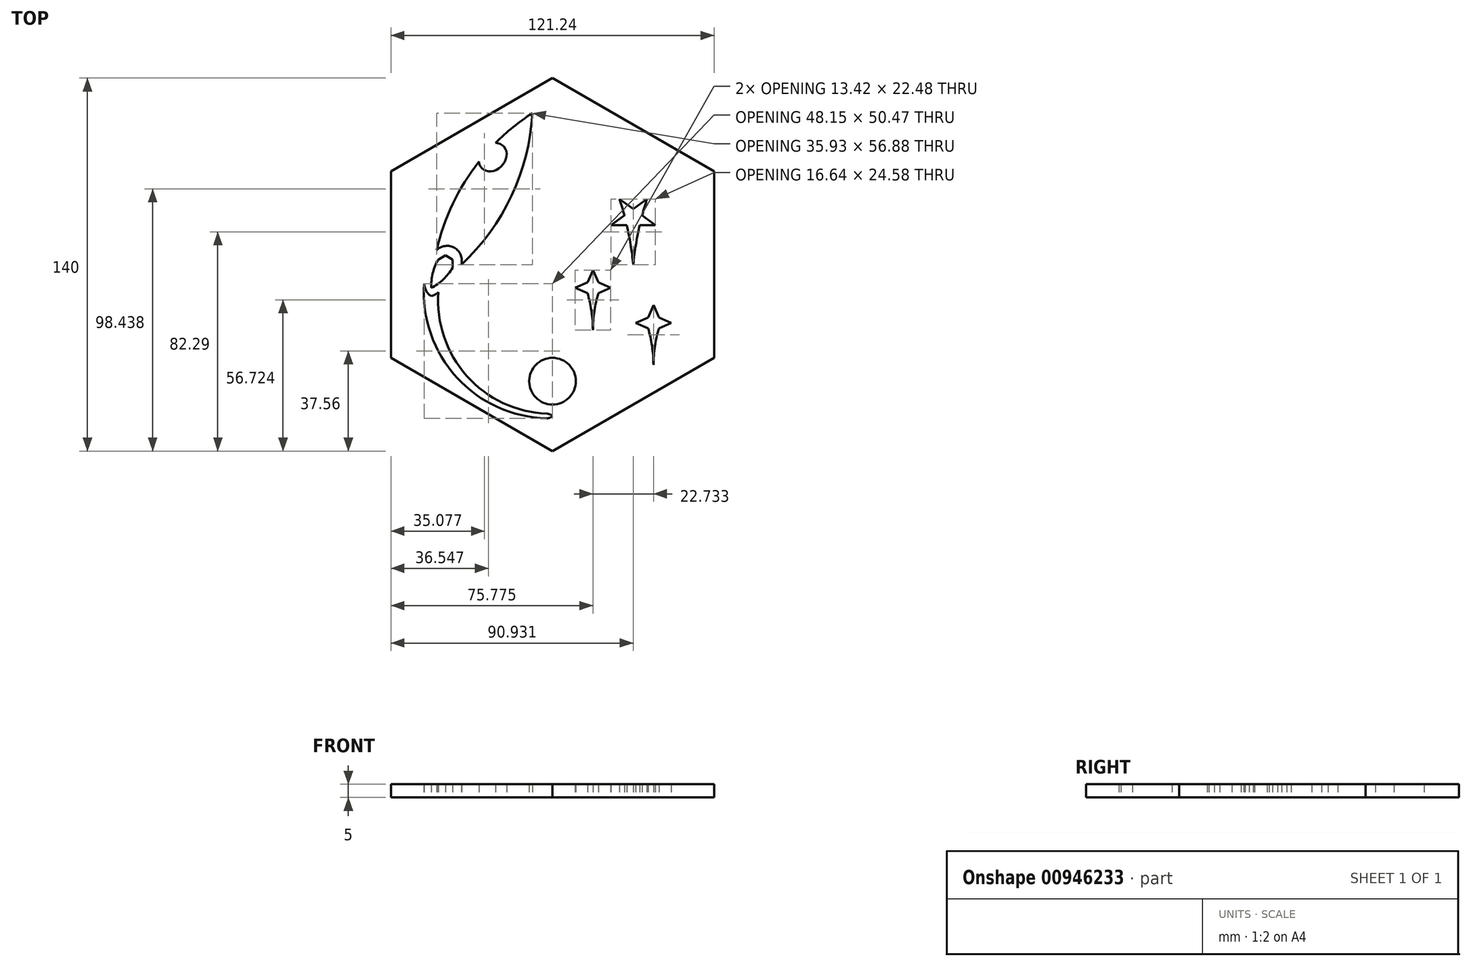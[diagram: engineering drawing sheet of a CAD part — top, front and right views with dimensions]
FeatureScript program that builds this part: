
annotation { "Feature Type Name" : "Feature", "Feature Type Description" : "" }
export const myFeature = defineFeature(function(context is Context, id is Id, definition is map)
    precondition{}
    {
        {
            var Q0;
            Q0=qCreatedBy(makeId("Top.planeOp"),FACE);
            var sketch = newSketch(context, id + "F0", { "sketchPlane" : qUnion([Q0])});
            skCircle(sketch, "E0.cCircle", {"center": v(0, 0) * mm, "radius": 60.62 * mm, "construction": true});
            skLineSegment(sketch, "E0.0", {"start": v(60.62, 35) * mm, "end": v(60.62, -35) * mm});
            skLineSegment(sketch, "E0.1", {"start": v(60.62, -35) * mm, "end": v(0, -70) * mm});
            skLineSegment(sketch, "E0.2", {"start": v(0, -70) * mm, "end": v(-60.62, -35) * mm});
            skLineSegment(sketch, "E0.3", {"start": v(-60.62, -35) * mm, "end": v(-60.62, 35) * mm});
            skLineSegment(sketch, "E0.4", {"start": v(-60.62, 35) * mm, "end": v(0, 70) * mm});
            skLineSegment(sketch, "E0.5", {"start": v(0, 70) * mm, "end": v(60.62, 35) * mm});
            skPoint(sketch, "E0.0.midPoint", {"position": v(60.62, 0) * mm});
            skLineSegment(sketch, "E1", {"start": v(0, 0) * mm, "end": v(0, -35) * mm, "construction": true});
            skLineSegment(sketch, "E2", {"start": v(-30.31, 17.5) * mm, "end": v(-60.62, 35) * mm, "construction": true});
            skLineSegment(sketch, "E3", {"start": v(0, 0) * mm, "end": v(60.62, 35) * mm, "construction": true});
            skLineSegment(sketch, "E4", {"start": v(60.62, -35) * mm, "end": v(15.16, -8.75) * mm, "construction": true});
            skLineSegment(sketch, "E5", {"start": v(0, -35) * mm, "end": v(30.31, 17.5) * mm, "construction": true});
            skLineSegment(sketch, "E6", {"start": v(0, -35) * mm, "end": v(0, -43.75) * mm, "construction": true});
            skLineSegment(sketch, "E7", {"start": v(0, -52.5) * mm, "end": v(0, -70) * mm, "construction": true});
            skLineSegment(sketch, "E8", {"start": v(0, -43.75) * mm, "end": v(0, -52.5) * mm, "construction": true});
            skCircle(sketch, "E9", {"center": v(0, -43.75) * mm, "radius": 8.75 * mm});
            skPoint(sketch, "E10", {"position": v(37.89, -21.88) * mm});
            skPoint(sketch, "E11", {"position": v(-30.31, 17.5) * mm});
            skLineSegment(sketch, "E12", {"start": v(-60.62, -35) * mm, "end": v(-45.47, -8.75) * mm, "construction": true});
            skLineSegment(sketch, "E13", {"start": v(0, 70) * mm, "end": v(-7.58, 56.88) * mm, "construction": true});
            skLineSegment(sketch, "E14", {"start": v(-45.47, -8.75) * mm, "end": v(-37.89, 4.37) * mm, "construction": true});
            skLineSegment(sketch, "E15", {"start": v(-15.16, 43.75) * mm, "end": v(-30.31, 17.5) * mm, "construction": true});
            skLineSegment(sketch, "E16", {"start": v(-7.58, 56.88) * mm, "end": v(-15.16, 43.75) * mm, "construction": true});
            skArc(sketch, "E17", {"start": v(-60.62, -16.52) * mm, "mid": v(-59.59, -16.11) * mm, "end": v(-58.56, -15.69) * mm, "construction": true});
            skLineSegment(sketch, "E18", {"start": v(-15.16, 8.75) * mm, "end": v(-30.31, 17.5) * mm, "construction": true});
            skLineSegment(sketch, "E19", {"start": v(0, 0) * mm, "end": v(-15.16, 8.75) * mm, "construction": true});
            skPoint(sketch, "E20", {"position": v(-22.73, 13.12) * mm});
            skArc(sketch, "E21.trimOffspring", {"start": v(-45.47, -8.75) * mm, "mid": v(-18.65, 19.52) * mm, "end": v(-7.58, 56.88) * mm});
            skArc(sketch, "E22.MirrorCS", {"start": v(-45.47, -8.75) * mm, "mid": v(-34.4, 28.6) * mm, "end": v(-7.58, 56.88) * mm});
            skLineSegment(sketch, "E23", {"start": v(-37.89, 4.37) * mm, "end": v(-34.1, 10.94) * mm, "construction": true});
            skLineSegment(sketch, "E24", {"start": v(-34.1, 10.94) * mm, "end": v(-30.31, 17.5) * mm, "construction": true});
            skCircle(sketch, "E25.cCircle", {"center": v(30.31, 17.5) * mm, "radius": 2.7 * mm, "construction": true});
            skLineSegment(sketch, "E25.0", {"start": v(35.45, 24.58) * mm, "end": v(30.31, 8.75) * mm});
            skLineSegment(sketch, "E25.1", {"start": v(38.63, 14.8) * mm, "end": v(21.99, 14.8) * mm});
            skLineSegment(sketch, "E25.2", {"start": v(30.31, 8.75) * mm, "end": v(25.17, 24.58) * mm});
            skLineSegment(sketch, "E25.3", {"start": v(21.99, 14.8) * mm, "end": v(35.45, 24.58) * mm});
            skLineSegment(sketch, "E25.4", {"start": v(25.17, 24.58) * mm, "end": v(38.63, 14.8) * mm});
            skPoint(sketch, "E25.0.midPoint", {"position": v(32.88, 16.66) * mm});
            skPoint(sketch, "E26.orphan", {"position": v(27.13, 18.53) * mm});
            skPoint(sketch, "E27.orphan", {"position": v(30.31, 20.84) * mm});
            skPoint(sketch, "E28.orphan", {"position": v(33.49, 18.53) * mm});
            skPoint(sketch, "E29.orphan", {"position": v(32.28, 14.8) * mm});
            skPoint(sketch, "E30.orphan", {"position": v(28.35, 14.8) * mm});
            skLineSegment(sketch, "E31", {"start": v(30.31, 17.5) * mm, "end": v(30.31, 0) * mm, "construction": true});
            skPoint(sketch, "E32", {"position": v(30.31, 8.75) * mm});
            skArc(sketch, "E33", {"start": v(30.31, 0) * mm, "mid": v(28.4, 12.43) * mm, "end": v(25.17, 24.58) * mm});
            skArc(sketch, "E34", {"start": v(35.45, 24.58) * mm, "mid": v(32.22, 12.43) * mm, "end": v(30.31, 0) * mm});
            skLineSegment(sketch, "E35", {"start": v(30.31, 17.5) * mm, "end": v(27.97, 18.85) * mm, "construction": true});
            skCircle(sketch, "E36", {"center": v(30.31, 17.5) * mm, "radius": 1.35 * mm, "construction": true});
            skPoint(sketch, "E37", {"position": v(29.14, 18.18) * mm});
            skCircle(sketch, "E38", {"center": v(30.31, 17.5) * mm, "radius": 2.03 * mm, "construction": true});
            skLineSegment(sketch, "E39", {"start": v(30.31, 17.5) * mm, "end": v(30.99, 18.67) * mm, "construction": true});
            skLineSegment(sketch, "E40", {"start": v(30.99, 18.67) * mm, "end": v(31.66, 19.84) * mm, "construction": true});
            skPoint(sketch, "E41", {"position": v(31.32, 19.26) * mm});
            skSolve(sketch);
        }
        {
            var Q0;
            Q0=qCreatedBy(makeId("Top.planeOp"),FACE);
            var sketch = newSketch(context, id + "F1", { "sketchPlane" : qUnion([Q0])});
            skPoint(sketch, "E42.0", {"position": v(15.16, -8.75) * mm});
            skLineSegment(sketch, "E43.0", {"start": v(0, -70) * mm, "end": v(-60.62, -35) * mm});
            skLineSegment(sketch, "E44.0", {"start": v(-60.62, -35) * mm, "end": v(-60.62, 35) * mm});
            skLineSegment(sketch, "E45.0", {"start": v(-60.62, 35) * mm, "end": v(0, 70) * mm});
            skLineSegment(sketch, "E46.0", {"start": v(0, 70) * mm, "end": v(60.62, 35) * mm});
            skLineSegment(sketch, "E47.0", {"start": v(60.62, 35) * mm, "end": v(60.62, -35) * mm});
            skLineSegment(sketch, "E48.0", {"start": v(60.62, -35) * mm, "end": v(0, -70) * mm});
            skArc(sketch, "E49.0", {"start": v(-45.47, -8.75) * mm, "mid": v(-18.65, 19.52) * mm, "end": v(-7.58, 56.88) * mm});
            skArc(sketch, "E50.0", {"start": v(-45.47, -8.75) * mm, "mid": v(-34.4, 28.6) * mm, "end": v(-7.58, 56.88) * mm});
            skCircle(sketch, "E51.cCircle", {"center": v(15.16, -8.75) * mm, "radius": 2.03 * mm, "construction": true});
            skLineSegment(sketch, "E51.3", {"start": v(13.13, -6.72) * mm, "end": v(17.18, -6.72) * mm});
            skPoint(sketch, "E51.0.midPoint", {"position": v(17.18, -8.75) * mm});
            skCircle(sketch, "E52.cCircle", {"center": v(15.16, -5.55) * mm, "radius": 1.17 * mm, "construction": true});
            skLineSegment(sketch, "E52.1", {"start": v(13.13, -6.72) * mm, "end": v(15.16, -3.2) * mm});
            skLineSegment(sketch, "E52.2", {"start": v(15.16, -3.2) * mm, "end": v(17.18, -6.72) * mm});
            skPoint(sketch, "E52.0.midPoint", {"position": v(15.16, -6.72) * mm});
            skLineSegment(sketch, "E53", {"start": v(15.16, -5.55) * mm, "end": v(15.16, -0.87) * mm, "construction": true});
            skPoint(sketch, "E54", {"position": v(15.16, -3.2) * mm});
            skLineSegment(sketch, "E55", {"start": v(15.16, -3.2) * mm, "end": v(15.16, -0.87) * mm, "construction": true});
            skLineSegment(sketch, "E56", {"start": v(17.18, -6.72) * mm, "end": v(15.16, -2.04) * mm});
            skLineSegment(sketch, "E57", {"start": v(13.13, -6.72) * mm, "end": v(15.16, -2.04) * mm});
            skLineSegment(sketch, "E58.1.0", {"start": v(13.13, -6.72) * mm, "end": v(8.44, -8.75) * mm});
            skPoint(sketch, "E58.1.1", {"position": v(13.13, -8.75) * mm});
            skLineSegment(sketch, "E58.1.2", {"start": v(9.62, -8.75) * mm, "end": v(13.13, -6.72) * mm});
            skLineSegment(sketch, "E58.1.3", {"start": v(9.62, -8.75) * mm, "end": v(7.27, -8.75) * mm, "construction": true});
            skLineSegment(sketch, "E58.1.4", {"start": v(11.96, -8.75) * mm, "end": v(7.27, -8.75) * mm, "construction": true});
            skLineSegment(sketch, "E58.1.5", {"start": v(13.13, -10.78) * mm, "end": v(8.44, -8.75) * mm});
            skLineSegment(sketch, "E58.1.6", {"start": v(13.13, -10.78) * mm, "end": v(13.13, -6.72) * mm});
            skCircle(sketch, "E58.1.7", {"center": v(11.96, -8.75) * mm, "radius": 1.17 * mm, "construction": true});
            skPoint(sketch, "E58.1.8", {"position": v(9.62, -8.75) * mm});
            skLineSegment(sketch, "E58.1.9", {"start": v(13.13, -10.78) * mm, "end": v(9.62, -8.75) * mm});
            skLineSegment(sketch, "E58.2.0", {"start": v(13.13, -10.78) * mm, "end": v(15.16, -15.46) * mm});
            skPoint(sketch, "E58.2.1", {"position": v(15.16, -10.78) * mm});
            skLineSegment(sketch, "E58.2.2", {"start": v(15.16, -14.3) * mm, "end": v(13.13, -10.78) * mm});
            skLineSegment(sketch, "E58.2.3", {"start": v(15.16, -14.3) * mm, "end": v(15.16, -16.63) * mm, "construction": true});
            skLineSegment(sketch, "E58.2.4", {"start": v(15.16, -11.95) * mm, "end": v(15.16, -16.63) * mm, "construction": true});
            skLineSegment(sketch, "E58.2.5", {"start": v(17.18, -10.78) * mm, "end": v(15.16, -15.46) * mm});
            skLineSegment(sketch, "E58.2.6", {"start": v(17.18, -10.78) * mm, "end": v(13.13, -10.78) * mm});
            skCircle(sketch, "E58.2.7", {"center": v(15.16, -11.95) * mm, "radius": 1.17 * mm, "construction": true});
            skPoint(sketch, "E58.2.8", {"position": v(15.16, -14.3) * mm});
            skLineSegment(sketch, "E58.2.9", {"start": v(17.18, -10.78) * mm, "end": v(15.16, -14.3) * mm});
            skLineSegment(sketch, "E58.3.0", {"start": v(17.18, -10.78) * mm, "end": v(21.87, -8.75) * mm});
            skLineSegment(sketch, "E58.3.2", {"start": v(20.7, -8.75) * mm, "end": v(17.18, -10.78) * mm});
            skLineSegment(sketch, "E58.3.3", {"start": v(20.7, -8.75) * mm, "end": v(23.04, -8.75) * mm, "construction": true});
            skLineSegment(sketch, "E58.3.4", {"start": v(18.35, -8.75) * mm, "end": v(23.04, -8.75) * mm, "construction": true});
            skLineSegment(sketch, "E58.3.5", {"start": v(17.18, -6.72) * mm, "end": v(21.87, -8.75) * mm});
            skLineSegment(sketch, "E58.3.6", {"start": v(17.18, -6.72) * mm, "end": v(17.18, -10.78) * mm});
            skCircle(sketch, "E58.3.7", {"center": v(18.35, -8.75) * mm, "radius": 1.17 * mm, "construction": true});
            skPoint(sketch, "E58.3.8", {"position": v(20.7, -8.75) * mm});
            skLineSegment(sketch, "E58.3.9", {"start": v(17.18, -6.72) * mm, "end": v(20.7, -8.75) * mm});
            skLineSegment(sketch, "E59", {"start": v(15.16, -8.75) * mm, "end": v(15.16, -24.51) * mm, "construction": true});
            skArc(sketch, "E60", {"start": v(17.18, -10.78) * mm, "mid": v(15.67, -17.57) * mm, "end": v(15.16, -24.51) * mm});
            skArc(sketch, "E61", {"start": v(15.16, -24.51) * mm, "mid": v(14.65, -17.57) * mm, "end": v(13.13, -10.78) * mm});
            skPoint(sketch, "E62.0", {"position": v(37.89, -21.88) * mm});
            skCircle(sketch, "E63.cCircle", {"center": v(37.89, -21.88) * mm, "radius": 2.03 * mm, "construction": true});
            skLineSegment(sketch, "E63.0", {"start": v(39.92, -19.85) * mm, "end": v(39.92, -23.9) * mm});
            skLineSegment(sketch, "E63.1", {"start": v(39.92, -23.9) * mm, "end": v(35.86, -23.9) * mm});
            skLineSegment(sketch, "E63.2", {"start": v(35.86, -23.9) * mm, "end": v(35.86, -19.85) * mm});
            skLineSegment(sketch, "E63.3", {"start": v(35.86, -19.85) * mm, "end": v(39.92, -19.85) * mm});
            skPoint(sketch, "E63.0.midPoint", {"position": v(39.92, -21.88) * mm});
            skCircle(sketch, "E64.cCircle", {"center": v(37.89, -18.68) * mm, "radius": 1.17 * mm, "construction": true});
            skLineSegment(sketch, "E64.0", {"start": v(35.86, -19.85) * mm, "end": v(37.89, -16.33) * mm});
            skLineSegment(sketch, "E64.1", {"start": v(37.89, -16.33) * mm, "end": v(39.92, -19.85) * mm});
            skLineSegment(sketch, "E64.2", {"start": v(39.92, -19.85) * mm, "end": v(35.86, -19.85) * mm});
            skPoint(sketch, "E64.0.midPoint", {"position": v(36.87, -18.1) * mm});
            skLineSegment(sketch, "E65", {"start": v(37.89, -18.68) * mm, "end": v(37.89, -14) * mm, "construction": true});
            skLineSegment(sketch, "E66", {"start": v(37.89, -16.33) * mm, "end": v(37.89, -14) * mm, "construction": true});
            skLineSegment(sketch, "E67", {"start": v(39.92, -19.85) * mm, "end": v(37.89, -15.16) * mm});
            skLineSegment(sketch, "E68", {"start": v(35.86, -19.85) * mm, "end": v(37.89, -15.16) * mm});
            skLineSegment(sketch, "E69.1.0", {"start": v(35.86, -23.9) * mm, "end": v(32.35, -21.87) * mm});
            skLineSegment(sketch, "E69.1.1", {"start": v(34.69, -21.87) * mm, "end": v(30, -21.88) * mm, "construction": true});
            skLineSegment(sketch, "E69.1.2", {"start": v(32.35, -21.88) * mm, "end": v(35.86, -19.85) * mm});
            skLineSegment(sketch, "E69.1.3", {"start": v(32.35, -21.88) * mm, "end": v(30, -21.88) * mm, "construction": true});
            skLineSegment(sketch, "E69.1.4", {"start": v(35.86, -23.9) * mm, "end": v(31.18, -21.88) * mm});
            skPoint(sketch, "E69.1.5", {"position": v(34.1, -22.89) * mm});
            skLineSegment(sketch, "E69.1.6", {"start": v(35.86, -19.85) * mm, "end": v(35.86, -23.9) * mm});
            skCircle(sketch, "E69.1.7", {"center": v(34.69, -21.87) * mm, "radius": 1.17 * mm, "construction": true});
            skLineSegment(sketch, "E69.1.8", {"start": v(35.86, -19.85) * mm, "end": v(31.18, -21.88) * mm});
            skLineSegment(sketch, "E69.2.0", {"start": v(39.92, -23.9) * mm, "end": v(37.89, -27.42) * mm});
            skLineSegment(sketch, "E69.2.1", {"start": v(37.89, -25.07) * mm, "end": v(37.89, -29.76) * mm, "construction": true});
            skLineSegment(sketch, "E69.2.2", {"start": v(37.89, -27.42) * mm, "end": v(35.86, -23.9) * mm});
            skLineSegment(sketch, "E69.2.3", {"start": v(37.89, -27.42) * mm, "end": v(37.89, -29.76) * mm, "construction": true});
            skLineSegment(sketch, "E69.2.4", {"start": v(39.92, -23.9) * mm, "end": v(37.89, -28.59) * mm});
            skPoint(sketch, "E69.2.5", {"position": v(38.9, -25.66) * mm});
            skLineSegment(sketch, "E69.2.6", {"start": v(35.86, -23.9) * mm, "end": v(39.92, -23.9) * mm});
            skCircle(sketch, "E69.2.7", {"center": v(37.89, -25.07) * mm, "radius": 1.17 * mm, "construction": true});
            skLineSegment(sketch, "E69.2.8", {"start": v(35.86, -23.9) * mm, "end": v(37.89, -28.59) * mm});
            skLineSegment(sketch, "E69.3.0", {"start": v(39.92, -19.85) * mm, "end": v(43.43, -21.88) * mm});
            skLineSegment(sketch, "E69.3.1", {"start": v(41.09, -21.88) * mm, "end": v(45.77, -21.87) * mm, "construction": true});
            skLineSegment(sketch, "E69.3.2", {"start": v(43.43, -21.87) * mm, "end": v(39.92, -23.9) * mm});
            skLineSegment(sketch, "E69.3.3", {"start": v(43.43, -21.87) * mm, "end": v(45.77, -21.87) * mm, "construction": true});
            skLineSegment(sketch, "E69.3.4", {"start": v(39.92, -19.85) * mm, "end": v(44.6, -21.88) * mm});
            skPoint(sketch, "E69.3.5", {"position": v(41.67, -20.86) * mm});
            skLineSegment(sketch, "E69.3.6", {"start": v(39.92, -23.9) * mm, "end": v(39.92, -19.85) * mm});
            skCircle(sketch, "E69.3.7", {"center": v(41.09, -21.88) * mm, "radius": 1.17 * mm, "construction": true});
            skLineSegment(sketch, "E69.3.8", {"start": v(39.92, -23.9) * mm, "end": v(44.6, -21.87) * mm});
            skLineSegment(sketch, "E70", {"start": v(37.89, -21.88) * mm, "end": v(37.89, -37.64) * mm, "construction": true});
            skSolve(sketch);
        }
        {
            var Q0;
            Q0=makeQuery(id+"F0.imprint","IMPRINT",FACE,{"disambiguationData":[TD([[makeQuery(id+"F0.imprint","IMPRINT",EDGE,{"derivedFrom":sQuery(id+"F0.wireOp",EDGE,"E0.0")}),-1.0]])]});
            var sketch = newSketch(context, id + "F2", { "sketchPlane" : qUnion([Q0])});
            skPoint(sketch, "E71.0", {"position": v(35.86, -23.9) * mm});
            skPoint(sketch, "E72.0", {"position": v(39.92, -23.9) * mm});
            skPoint(sketch, "E73.0", {"position": v(37.89, -37.64) * mm});
            skArc(sketch, "E74", {"start": v(37.89, -37.64) * mm, "mid": v(37.38, -30.7) * mm, "end": v(35.86, -23.9) * mm});
            skLineSegment(sketch, "E75.0", {"start": v(37.89, -21.88) * mm, "end": v(37.89, -37.64) * mm, "construction": true});
            skArc(sketch, "E76", {"start": v(39.92, -23.9) * mm, "mid": v(38.4, -30.7) * mm, "end": v(37.89, -37.64) * mm});
            skSolve(sketch);
        }
        {
            var Q0;
            Q0=makeQuery(id+"F0.imprint","IMPRINT",FACE,{"disambiguationData":[TD([[makeQuery(id+"F0.imprint","IMPRINT",EDGE,{"derivedFrom":sQuery(id+"F0.wireOp",EDGE,"E0.0")}),-1.0]])]});
            var sketch = newSketch(context, id + "F3", { "sketchPlane" : qUnion([Q0])});
            skArc(sketch, "E77.0", {"start": v(-43.5, 5.36) * mm, "mid": v(-30.57, 34.63) * mm, "end": v(-7.58, 56.88) * mm});
            skArc(sketch, "E77.1", {"start": v(-34.23, 0) * mm, "mid": v(-15.35, 25.84) * mm, "end": v(-7.58, 56.88) * mm});
            skArc(sketch, "E78", {"start": v(-34.23, 0) * mm, "mid": v(-36.78, 6.3) * mm, "end": v(-43.5, 5.36) * mm});
            skLineSegment(sketch, "E79", {"start": v(-34.23, 0) * mm, "end": v(-36.55, 1.34) * mm, "construction": true});
            skLineSegment(sketch, "E80", {"start": v(-38.87, 2.68) * mm, "end": v(-43.5, 5.36) * mm, "construction": true});
            skLineSegment(sketch, "E81", {"start": v(-36.55, 1.34) * mm, "end": v(-38.87, 2.68) * mm, "construction": true});
            skLineSegment(sketch, "E82", {"start": v(-38.87, 2.68) * mm, "end": v(-40.2, 0.36) * mm, "construction": true});
            skPoint(sketch, "E83.orphan", {"position": v(-45.47, -8.75) * mm});
            skCircle(sketch, "E84.cCircle", {"center": v(-40.2, 0.36) * mm, "radius": 2.68 * mm, "construction": true});
            skLineSegment(sketch, "E84.2", {"start": v(-42.89, 1.9) * mm, "end": v(-40.2, 3.45) * mm});
            skLineSegment(sketch, "E84.3", {"start": v(-40.2, 3.45) * mm, "end": v(-37.53, 1.9) * mm});
            skLineSegment(sketch, "E84.4", {"start": v(-37.53, 1.9) * mm, "end": v(-37.53, -1.19) * mm});
            skPoint(sketch, "E84.0.midPoint", {"position": v(-41.55, -1.96) * mm});
            skArc(sketch, "E85", {"start": v(-45.47, -8.75) * mm, "mid": v(-40.95, -5.54) * mm, "end": v(-37.53, -1.19) * mm, "construction": true});
            skArc(sketch, "E86.MirrorCS", {"start": v(-45.47, -8.75) * mm, "mid": v(-44.94, -3.24) * mm, "end": v(-42.89, 1.9) * mm, "construction": true});
            skLineSegment(sketch, "E87", {"start": v(-36.22, 1.9) * mm, "end": v(-42.37, -8.75) * mm, "construction": true});
            skLineSegment(sketch, "E88", {"start": v(-35.74, 1.9) * mm, "end": v(-41.9, -8.75) * mm, "construction": true});
            skCircle(sketch, "E89.0", {"center": v(0, -43.75) * mm, "radius": 8.75 * mm});
            skLineSegment(sketch, "E90", {"start": v(0, -43.75) * mm, "end": v(-8.75, -43.75) * mm, "construction": true});
            skLineSegment(sketch, "E91", {"start": v(-17.5, -43.75) * mm, "end": v(-8.75, -43.75) * mm, "construction": true});
            skPoint(sketch, "E92", {"position": v(-44.94, -3.24) * mm});
            skPoint(sketch, "E93", {"position": v(-40.95, -5.54) * mm});
            skLineSegment(sketch, "E94", {"start": v(-48.15, -7.2) * mm, "end": v(-45.47, -8.75) * mm, "construction": true});
            skLineSegment(sketch, "E95", {"start": v(-37.53, -1.19) * mm, "end": v(-42.79, -10.3) * mm, "construction": true});
            skLineSegment(sketch, "E96", {"start": v(0, -43.75) * mm, "end": v(0, -52.5) * mm, "construction": true});
            skLineSegment(sketch, "E97", {"start": v(0, -43.75) * mm, "end": v(-6.19, -49.94) * mm, "construction": true});
            skLineSegment(sketch, "E98", {"start": v(0, -52.5) * mm, "end": v(-8.75, -43.75) * mm, "construction": true});
            skPoint(sketch, "E99", {"position": v(-4.38, -48.13) * mm});
            skLineSegment(sketch, "E100", {"start": v(0, -43.75) * mm, "end": v(-16.17, -50.45) * mm, "construction": true});
            skLineSegment(sketch, "E101", {"start": v(-6.19, -49.94) * mm, "end": v(-8.75, -43.75) * mm, "construction": true});
            skPoint(sketch, "E102", {"position": v(-7.47, -46.84) * mm});
            skCircle(sketch, "E103", {"center": v(0, -43.75) * mm, "radius": 17.5 * mm, "construction": true});
            skLineSegment(sketch, "E104", {"start": v(-16.17, -50.45) * mm, "end": v(-16.83, -47.1) * mm, "construction": true});
            skPoint(sketch, "E105", {"position": v(-16.83, -47.1) * mm});
            skLineSegment(sketch, "E106", {"start": v(0, -43.75) * mm, "end": v(-12.63, -46.26) * mm, "construction": true});
            skLineSegment(sketch, "E107", {"start": v(-45.47, -8.75) * mm, "end": v(-44.94, -3.24) * mm, "construction": true});
            skLineSegment(sketch, "E108", {"start": v(-40.95, -5.54) * mm, "end": v(-45.47, -8.75) * mm, "construction": true});
            skPoint(sketch, "E109", {"position": v(-45.2, -6) * mm});
            skPoint(sketch, "E110", {"position": v(-43.2, -7.15) * mm});
            skLineSegment(sketch, "E111", {"start": v(-13.13, -43.75) * mm, "end": v(-12.63, -46.26) * mm, "construction": true});
            skPoint(sketch, "E112.0", {"position": v(-15.16, 43.75) * mm});
            skPoint(sketch, "E113.0", {"position": v(-30.31, 17.5) * mm});
            skLineSegment(sketch, "E114", {"start": v(-15.16, 43.75) * mm, "end": v(-18.94, 37.19) * mm, "construction": true});
            skLineSegment(sketch, "E115", {"start": v(-22.73, 30.62) * mm, "end": v(-30.31, 17.5) * mm, "construction": true});
            skLineSegment(sketch, "E116", {"start": v(-18.94, 37.19) * mm, "end": v(-22.73, 30.62) * mm, "construction": true});
            skEllipse(sketch, "E117", {"center": v(-22.42, 40.3) * mm, "majorRadius": 5.8 * mm, "minorRadius": 4.67 * mm, "majorAxis": v(0.67, 0.74)});
            skPoint(sketch, "E118", {"position": v(-26.3, 35.97) * mm});
            skPoint(sketch, "E119", {"position": v(-18.55, 44.63) * mm});
            skLineSegment(sketch, "E120", {"start": v(-7.58, 56.88) * mm, "end": v(-27.47, 31.17) * mm, "construction": true});
            skEllipse(sketch, "E121", {"center": v(-22.73, 30.62) * mm, "majorRadius": 8.74 * mm, "minorRadius": 3.79 * mm, "majorAxis": v(0.87, -0.5), "construction": true});
            skPoint(sketch, "E122", {"position": v(-24.63, 27.34) * mm});
            skPoint(sketch, "E123", {"position": v(-30.3, 35) * mm});
            skLineSegment(sketch, "E124", {"start": v(-30.3, 35) * mm, "end": v(-27.47, 31.17) * mm, "construction": true});
            skPoint(sketch, "E125", {"position": v(-27.47, 31.17) * mm});
            skPoint(sketch, "E126", {"position": v(-20.84, 33.9) * mm});
            skPoint(sketch, "E127", {"position": v(-25.9, 43.42) * mm});
            skLineSegment(sketch, "E128", {"start": v(-27.47, 31.17) * mm, "end": v(-24.63, 27.34) * mm, "construction": true});
            skPoint(sketch, "E129", {"position": v(-28.89, 33.08) * mm});
            skLineSegment(sketch, "E130", {"start": v(-7.58, 56.88) * mm, "end": v(-28.89, 33.08) * mm, "construction": true});
            skPoint(sketch, "E131", {"position": v(-18.94, 37.19) * mm});
            skLineSegment(sketch, "E132", {"start": v(-45.47, -8.75) * mm, "end": v(-42.79, -10.3) * mm, "construction": true});
            skLineSegment(sketch, "E133", {"start": v(-16.83, -47.1) * mm, "end": v(-17.5, -43.75) * mm, "construction": true});
            skPoint(sketch, "E134", {"position": v(-17.17, -45.42) * mm});
            skPoint(sketch, "E135", {"position": v(-12.88, -45) * mm});
            skLineSegment(sketch, "E136", {"start": v(-12.88, -45) * mm, "end": v(-17.17, -45.42) * mm, "construction": true});
            skLineSegment(sketch, "E137", {"start": v(-12.63, -46.26) * mm, "end": v(-17.16, -47.16) * mm, "construction": true});
            skLineSegment(sketch, "E138", {"start": v(-13.13, -43.75) * mm, "end": v(-17.5, -43.75) * mm, "construction": true});
            skPoint(sketch, "E139", {"position": v(-15.31, -43.75) * mm});
            skPoint(sketch, "E140", {"position": v(-14.9, -46.71) * mm});
            skLineSegment(sketch, "E141", {"start": v(-14.9, -46.71) * mm, "end": v(-15.02, -45.21) * mm, "construction": true});
            skPoint(sketch, "E142", {"position": v(-14.96, -45.96) * mm});
            skArc(sketch, "E143", {"start": v(-17.17, -45.42) * mm, "mid": v(-16.01, -45.5) * mm, "end": v(-14.96, -45.96) * mm, "construction": true});
            skArc(sketch, "E144", {"start": v(-16.83, -47.1) * mm, "mid": v(-15.8, -46.7) * mm, "end": v(-14.96, -45.96) * mm, "construction": true});
            skPoint(sketch, "E145", {"position": v(-40.3, -35.38) * mm});
            skLineSegment(sketch, "E146", {"start": v(-40.3, -35.38) * mm, "end": v(-43.78, -37.93) * mm, "construction": true});
            skPoint(sketch, "E147", {"position": v(-42.04, -36.66) * mm});
            skArc(sketch, "E148", {"start": v(-45.47, -8.75) * mm, "mid": v(-41.85, -36.9) * mm, "end": v(-14.96, -45.96) * mm, "construction": true});
            skLineSegment(sketch, "E149", {"start": v(-46.6, -11.63) * mm, "end": v(-45.47, -8.75) * mm, "construction": true});
            skLineSegment(sketch, "E150", {"start": v(-45.47, -8.75) * mm, "end": v(-46.49, -5.83) * mm, "construction": true});
            skArc(sketch, "E151", {"start": v(-48.15, -7.2) * mm, "mid": v(-44.74, -36.77) * mm, "end": v(-16.83, -47.1) * mm, "construction": true});
            skArc(sketch, "E152", {"start": v(-42.79, -10.3) * mm, "mid": v(-40.3, -35.38) * mm, "end": v(-17.17, -45.42) * mm, "construction": true});
            skArc(sketch, "E153", {"start": v(-48.15, -7.2) * mm, "mid": v(-47.84, -9.58) * mm, "end": v(-46.6, -11.63) * mm});
            skArc(sketch, "E154", {"start": v(-46.6, -11.63) * mm, "mid": v(-44.57, -11.3) * mm, "end": v(-42.79, -10.3) * mm});
            skLineSegment(sketch, "E155", {"start": v(0, -52.5) * mm, "end": v(0, -61.25) * mm, "construction": true});
            skPoint(sketch, "E156", {"position": v(0, -56.88) * mm});
            skCircle(sketch, "E157", {"center": v(0, -45.94) * mm, "radius": 10.94 * mm, "construction": true});
            skArc(sketch, "E158", {"start": v(-40.2, 0.36) * mm, "mid": v(-34.97, -38.7) * mm, "end": v(0, -56.88) * mm, "construction": true});
            skCircle(sketch, "E159", {"center": v(-40.2, 0.36) * mm, "radius": 10.52 * mm, "construction": true});
            skArc(sketch, "E160", {"start": v(-42.89, 1.9) * mm, "mid": v(-43.62, -4) * mm, "end": v(-42.52, -9.84) * mm});
            skArc(sketch, "E161", {"start": v(-42.52, -9.84) * mm, "mid": v(-39.46, -5.84) * mm, "end": v(-37.53, -1.19) * mm});
            skSolve(sketch);
        }
        {
            var Q0;
            Q0=qCreatedBy(makeId("Top.planeOp"),FACE);
            var sketch = newSketch(context, id + "F4", { "sketchPlane" : qUnion([Q0])});
            skCircle(sketch, "E162.0", {"center": v(0, -43.75) * mm, "radius": 8.75 * mm, "construction": true});
            skPoint(sketch, "E163.0", {"position": v(-48.15, -7.2) * mm});
            skPoint(sketch, "E164.0", {"position": v(-42.79, -10.3) * mm});
            skLineSegment(sketch, "E165", {"start": v(0, -43.75) * mm, "end": v(0, -52.5) * mm, "construction": true});
            skLineSegment(sketch, "E166", {"start": v(0, -52.5) * mm, "end": v(0, -56.88) * mm, "construction": true});
            skLineSegment(sketch, "E167", {"start": v(0, -56.88) * mm, "end": v(0, -61.25) * mm, "construction": true});
            skLineSegment(sketch, "E168.0", {"start": v(-12.88, -45) * mm, "end": v(-15.02, -45.21) * mm, "construction": true});
            skLineSegment(sketch, "E169", {"start": v(-15.02, -45.21) * mm, "end": v(-17.17, -45.42) * mm, "construction": true});
            skLineSegment(sketch, "E170", {"start": v(0, -43.75) * mm, "end": v(-2.85, -61.02) * mm, "construction": true});
            skCircle(sketch, "E171.0", {"center": v(0, -43.75) * mm, "radius": 17.5 * mm, "construction": true});
            skLineSegment(sketch, "E172", {"start": v(0, -56.88) * mm, "end": v(-2.16, -56.82) * mm, "construction": true});
            skArc(sketch, "E173", {"start": v(-45.47, -8.75) * mm, "mid": v(-33.1, -42.6) * mm, "end": v(0, -56.88) * mm, "construction": true});
            skPoint(sketch, "E174.0", {"position": v(-45.47, -8.75) * mm});
            skLineSegment(sketch, "E175.0", {"start": v(-16.83, -47.1) * mm, "end": v(-17.17, -45.42) * mm, "construction": true});
            skLineSegment(sketch, "E176", {"start": v(-17.17, -45.42) * mm, "end": v(-17.5, -43.75) * mm, "construction": true});
            skLineSegment(sketch, "E177", {"start": v(-2.12, -55.97) * mm, "end": v(-2.2, -57.68) * mm, "construction": true});
            skPoint(sketch, "E178", {"position": v(-2.16, -56.82) * mm});
            skArc(sketch, "E179", {"start": v(0, -56.88) * mm, "mid": v(-0.97, -56.23) * mm, "end": v(-2.12, -55.97) * mm});
            skArc(sketch, "E180", {"start": v(-2.2, -57.68) * mm, "mid": v(-1.02, -57.48) * mm, "end": v(0, -56.88) * mm});
            skCircle(sketch, "E181", {"center": v(0, -45.94) * mm, "radius": 10.94 * mm, "construction": true});
            skArc(sketch, "E182", {"start": v(-42.79, -10.3) * mm, "mid": v(-32.17, -41.8) * mm, "end": v(-2.12, -55.97) * mm});
            skArc(sketch, "E183", {"start": v(-48.15, -7.2) * mm, "mid": v(-36, -42.3) * mm, "end": v(-2.2, -57.68) * mm});
            skArc(sketch, "E184", {"start": v(-45.54, -11.84) * mm, "mid": v(-44.05, -11.26) * mm, "end": v(-42.79, -10.3) * mm});
            skArc(sketch, "E185", {"start": v(-48.15, -7.2) * mm, "mid": v(-47.4, -9.84) * mm, "end": v(-45.54, -11.84) * mm});
            skLineSegment(sketch, "E186", {"start": v(-45.54, -11.84) * mm, "end": v(-45.47, -8.75) * mm, "construction": true});
            skSolve(sketch);
        }
        {
            var Q0;
            Q0=qCreatedBy(makeId("Top.planeOp"),FACE);
            var sketch = newSketch(context, id + "F5", { "sketchPlane" : qUnion([Q0])});
            skCircle(sketch, "E187.0", {"center": v(0, -43.75) * mm, "radius": 8.75 * mm});
            skLineSegment(sketch, "E188.0", {"start": v(60.62, -35) * mm, "end": v(0, -70) * mm});
            skLineSegment(sketch, "E189.0", {"start": v(60.62, 35) * mm, "end": v(60.62, -35) * mm});
            skLineSegment(sketch, "E190.0", {"start": v(0, 70) * mm, "end": v(60.62, 35) * mm});
            skLineSegment(sketch, "E191.0", {"start": v(-60.62, 35) * mm, "end": v(0, 70) * mm});
            skLineSegment(sketch, "E192.0", {"start": v(-60.62, -35) * mm, "end": v(-60.62, 35) * mm});
            skArc(sketch, "E193.0", {"start": v(-34.23, 0) * mm, "mid": v(-15.35, 25.84) * mm, "end": v(-7.58, 56.88) * mm});
            skArc(sketch, "E194.0", {"start": v(-43.5, 5.36) * mm, "mid": v(-37.41, 22.88) * mm, "end": v(-27.6, 38.63) * mm});
            skArc(sketch, "E195.0", {"start": v(-34.23, 0) * mm, "mid": v(-36.78, 6.3) * mm, "end": v(-43.5, 5.36) * mm});
            skLineSegment(sketch, "E196.0", {"start": v(-42.89, 1.9) * mm, "end": v(-40.2, 3.45) * mm});
            skArc(sketch, "E197.0", {"start": v(-45.47, -8.75) * mm, "mid": v(-44.94, -3.24) * mm, "end": v(-42.89, 1.9) * mm});
            skLineSegment(sketch, "E198.0", {"start": v(-40.2, 3.45) * mm, "end": v(-37.53, 1.9) * mm});
            skLineSegment(sketch, "E199.0", {"start": v(-37.53, 1.9) * mm, "end": v(-37.53, -1.19) * mm});
            skArc(sketch, "E200.0", {"start": v(-45.47, -8.75) * mm, "mid": v(-40.95, -5.54) * mm, "end": v(-37.53, -1.19) * mm});
            skArc(sketch, "E201.0", {"start": v(15.16, -24.51) * mm, "mid": v(14.65, -17.57) * mm, "end": v(13.13, -10.78) * mm});
            skArc(sketch, "E202.0", {"start": v(17.18, -10.78) * mm, "mid": v(15.67, -17.57) * mm, "end": v(15.16, -24.51) * mm});
            skLineSegment(sketch, "E203.0", {"start": v(17.18, -10.78) * mm, "end": v(21.87, -8.75) * mm});
            skLineSegment(sketch, "E204.0", {"start": v(17.18, -6.72) * mm, "end": v(21.87, -8.75) * mm});
            skLineSegment(sketch, "E205.0", {"start": v(17.18, -6.72) * mm, "end": v(15.16, -2.04) * mm});
            skLineSegment(sketch, "E206.0", {"start": v(13.13, -6.72) * mm, "end": v(15.16, -2.04) * mm});
            skLineSegment(sketch, "E207.0", {"start": v(13.13, -6.72) * mm, "end": v(8.44, -8.75) * mm});
            skLineSegment(sketch, "E208.0", {"start": v(13.13, -10.78) * mm, "end": v(8.44, -8.75) * mm});
            skArc(sketch, "E209.0", {"start": v(39.92, -23.9) * mm, "mid": v(38.4, -30.7) * mm, "end": v(37.89, -37.64) * mm});
            skArc(sketch, "E210.0", {"start": v(37.89, -37.64) * mm, "mid": v(37.38, -30.7) * mm, "end": v(35.86, -23.9) * mm});
            skLineSegment(sketch, "E211.0", {"start": v(35.86, -23.9) * mm, "end": v(31.18, -21.88) * mm});
            skLineSegment(sketch, "E212.0", {"start": v(35.86, -19.85) * mm, "end": v(31.18, -21.88) * mm});
            skLineSegment(sketch, "E213.0", {"start": v(35.86, -19.85) * mm, "end": v(37.89, -15.16) * mm});
            skLineSegment(sketch, "E214.0", {"start": v(39.92, -19.85) * mm, "end": v(37.89, -15.16) * mm});
            skLineSegment(sketch, "E215.0", {"start": v(39.92, -19.85) * mm, "end": v(44.6, -21.88) * mm});
            skLineSegment(sketch, "E216.0", {"start": v(39.92, -23.9) * mm, "end": v(44.6, -21.87) * mm});
            skLineSegment(sketch, "E217.0", {"start": v(21.99, 14.8) * mm, "end": v(26.98, 18.42) * mm});
            skLineSegment(sketch, "E218.0", {"start": v(25.17, 24.58) * mm, "end": v(30.31, 20.84) * mm});
            skArc(sketch, "E219.0", {"start": v(30.31, 0) * mm, "mid": v(29.33, 7.44) * mm, "end": v(27.88, 14.8) * mm});
            skArc(sketch, "E220.0", {"start": v(35.45, 24.58) * mm, "mid": v(34.5, 21.51) * mm, "end": v(33.64, 18.42) * mm});
            skLineSegment(sketch, "E221.0", {"start": v(38.63, 14.8) * mm, "end": v(32.74, 14.8) * mm});
            skLineSegment(sketch, "E222.trimOffspring", {"start": v(27.88, 14.8) * mm, "end": v(21.99, 14.8) * mm});
            skArc(sketch, "E223.trimOffspring", {"start": v(26.98, 18.42) * mm, "mid": v(26.12, 21.51) * mm, "end": v(25.17, 24.58) * mm});
            skLineSegment(sketch, "E224.trimOffspring", {"start": v(30.31, 20.84) * mm, "end": v(35.45, 24.58) * mm});
            skLineSegment(sketch, "E225.trimOffspring", {"start": v(33.64, 18.42) * mm, "end": v(38.63, 14.8) * mm});
            skArc(sketch, "E226.trimOffspring", {"start": v(32.74, 14.8) * mm, "mid": v(31.29, 7.44) * mm, "end": v(30.31, 0) * mm});
            skEllipticalArc(sketch, "E227.0", {});
            skArc(sketch, "E228.trimOffspring", {"start": v(-21.4, 45.63) * mm, "mid": v(-14.79, 51.62) * mm, "end": v(-7.58, 56.88) * mm});
            skLineSegment(sketch, "E229.0.0", {"start": v(60.62, 35) * mm, "end": v(0, 70) * mm});
            skLineSegment(sketch, "E229.0.1", {"start": v(0, 70) * mm, "end": v(-60.62, 35) * mm});
            skLineSegment(sketch, "E229.0.2", {"start": v(-60.62, 35) * mm, "end": v(-60.62, -35) * mm});
            skLineSegment(sketch, "E229.0.4", {"start": v(0, -70) * mm, "end": v(60.62, -35) * mm});
            skLineSegment(sketch, "E229.0.5", {"start": v(60.62, -35) * mm, "end": v(60.62, 35) * mm});
            skLineSegment(sketch, "E230.0.3", {"start": v(-60.62, -35) * mm, "end": v(0, -70) * mm});
            skArc(sketch, "E231.0", {"start": v(-45.54, -11.84) * mm, "mid": v(-44.05, -11.26) * mm, "end": v(-42.79, -10.3) * mm});
            skArc(sketch, "E232.0", {"start": v(-48.15, -7.2) * mm, "mid": v(-47.4, -9.84) * mm, "end": v(-45.54, -11.84) * mm});
            skArc(sketch, "E233.0", {"start": v(-48.15, -7.2) * mm, "mid": v(-36, -42.3) * mm, "end": v(-2.2, -57.68) * mm});
            skArc(sketch, "E234.0", {"start": v(-42.79, -10.3) * mm, "mid": v(-32.17, -41.8) * mm, "end": v(-2.12, -55.97) * mm});
            skArc(sketch, "E235.0", {"start": v(0, -56.88) * mm, "mid": v(-0.97, -56.23) * mm, "end": v(-2.12, -55.97) * mm});
            skArc(sketch, "E236.0", {"start": v(-2.2, -57.68) * mm, "mid": v(-1.02, -57.48) * mm, "end": v(0, -56.88) * mm});
            const initialGuessF5  = {"E227.0": [-0.022421108092777586, 0.040301324675147666, 0.6671519415157839, 0.7449216649633169, 0.005809593947329204, 0.004667339598941902, 2.51368173577678, 0.6416830810560054]};
            skSetInitialGuess(sketch, initialGuessF5);
            skSolve(sketch);
        }
        {
            var Q0;
            Q0=makeQuery(id+"F5.imprint","IMPRINT",FACE,{"disambiguationData":[TD([[makeQuery(id+"F5.imprint","IMPRINT",EDGE,{"derivedFrom":sQuery(id+"F5.wireOp",EDGE,"E187.0")}),-1.0]])]});
            extrude(context, id + "F6", {"entities" : qUnion([Q0]), "depth" : 5 * mm, "offsetDistance" : 25 * mm});
        }
    });
